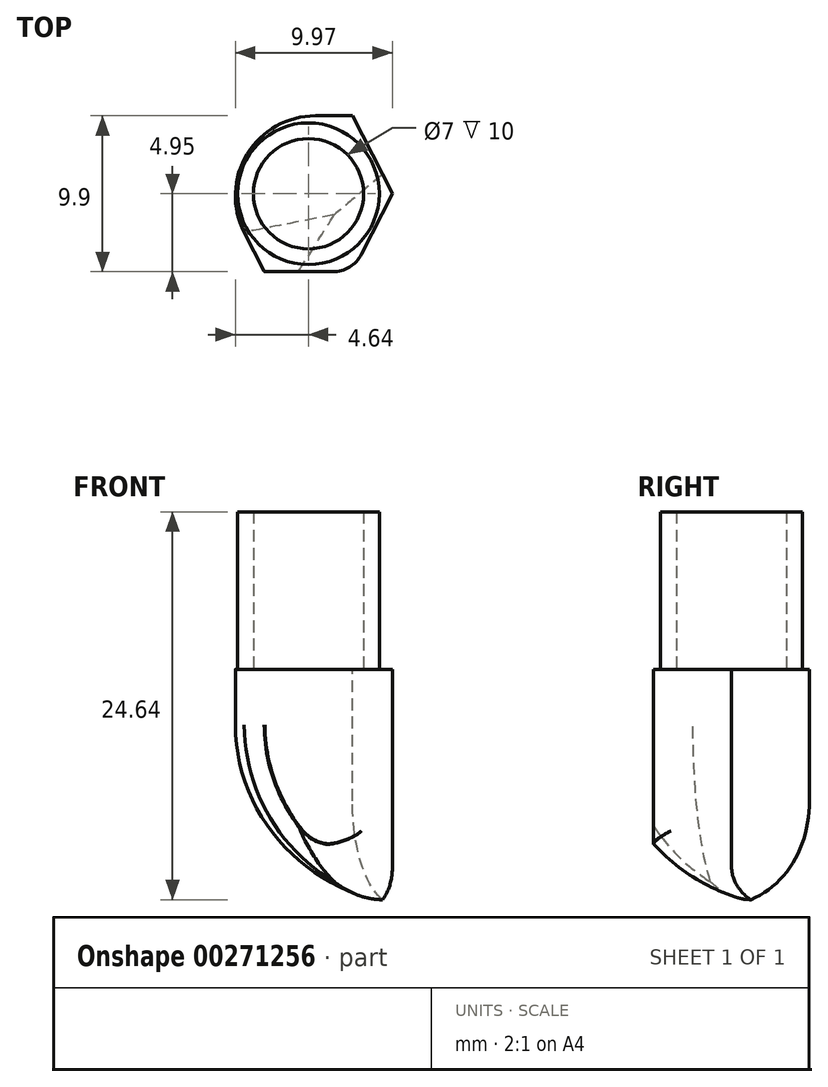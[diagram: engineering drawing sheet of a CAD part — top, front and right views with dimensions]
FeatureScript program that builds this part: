
annotation { "Feature Type Name" : "Feature", "Feature Type Description" : "" }
export const myFeature = defineFeature(function(context is Context, id is Id, definition is map)
    precondition{}
    {
        {
            var Q0;
            Q0=qCreatedBy(makeId("Top.planeOp"),FACE);
            var sketch = newSketch(context, id + "F0", { "sketchPlane" : qUnion([Q0])});
            skCircle(sketch, "E0", {"center": v(0, 0) * mm, "radius": 4.5 * mm});
            skCircle(sketch, "E1.0", {"center": v(0, 0) * mm, "radius": 3.5 * mm});
            skSolve(sketch);
        }
        {
            var Q0;
            Q0 = qSketchRegion(id + "F0", true);
            extrude(context, id + "F1", {"entities" : qUnion([Q0]), "depth" : 10 * mm});
        }
        {
            var Q0;
            Q0=qCreatedBy(makeId("Top.planeOp"),FACE);
            var sketch = newSketch(context, id + "F2", { "sketchPlane" : qUnion([Q0])});
            skLineSegment(sketch, "E2", {"start": v(0, 0) * mm, "end": v(0, -4.95) * mm});
            skLineSegment(sketch, "E3", {"start": v(0, -4.95) * mm, "end": v(0, 0) * mm});
            skLineSegment(sketch, "E4", {"start": v(0, 0) * mm, "end": v(0, 4.95) * mm});
            skLineSegment(sketch, "E5", {"start": v(0, 4.95) * mm, "end": v(2.8, 4.95) * mm});
            skLineSegment(sketch, "E6", {"start": v(2.8, 4.95) * mm, "end": v(2.8, -4.95) * mm});
            skLineSegment(sketch, "E7", {"start": v(2.8, -4.95) * mm, "end": v(0, -4.95) * mm});
            skLineSegment(sketch, "E8", {"start": v(0, -4.95) * mm, "end": v(-2.8, -4.95) * mm});
            skLineSegment(sketch, "E9", {"start": v(-2.8, -4.95) * mm, "end": v(-2.8, 4.95) * mm});
            skLineSegment(sketch, "E10", {"start": v(-2.8, 4.95) * mm, "end": v(0, 4.95) * mm});
            skLineSegment(sketch, "E11", {"start": v(-2.8, 0) * mm, "end": v(-5.33, 0) * mm});
            skLineSegment(sketch, "E12", {"start": v(-5.33, 0) * mm, "end": v(0, 0) * mm});
            skLineSegment(sketch, "E13", {"start": v(2.8, 0) * mm, "end": v(5.33, 0) * mm});
            skPoint(sketch, "E13.endSnap0", {"position": v(2.8, 0) * mm});
            skLineSegment(sketch, "E14", {"start": v(5.33, 0) * mm, "end": v(2.8, 0) * mm});
            skLineSegment(sketch, "E15", {"start": v(-2.8, 4.95) * mm, "end": v(-5.33, 0) * mm});
            skLineSegment(sketch, "E16", {"start": v(-2.8, -4.95) * mm, "end": v(-5.33, 0) * mm});
            skLineSegment(sketch, "E17", {"start": v(2.8, 4.95) * mm, "end": v(5.33, 0) * mm});
            skLineSegment(sketch, "E18", {"start": v(5.33, 0) * mm, "end": v(2.8, -4.95) * mm});
            skSolve(sketch);
        }
        {
            var Q0;
            Q0 = qSketchRegion(id + "F2", true);
            extrude(context, id + "F3", {"entities" : qUnion([Q0]), "operationType" : NewBodyOperationType.ADD, "oppositeDirection" : true, "depth" : 15 * mm});
        }
        {
            var Q0;
            Q0=makeQuery(id+"F3.opExtrude","CAP_EDGE",EDGE,{"disambiguationData":[OSD([sQuery(id+"F2.wireOp",EDGE,"E16")])],"isStart":false});
            fillet(context, id + "F4", {"entities" : qUnion([Q0]), "radius" : 11.65 * mm, "tangentPropagation" : true, "allowEdgeOverflow" : false});
        }
        {
            var Q0;
            Q0=makeQuery(id+"F4.opFillet","BLEND_EDGE",EDGE,{"blendedFrom":[makeQuery(id+"F3.opExtrude","CAP_EDGE",EDGE,{"disambiguationData":[OSD([sQuery(id+"F2.wireOp",EDGE,"E16")])],"isStart":false}),makeQuery(id+"F3.opExtrude","SWEPT_FACE",FACE,{"disambiguationData":[OSD([sQuery(id+"F2.wireOp",EDGE,"E7"),sQuery(id+"F2.wireOp",EDGE,"E8")])]})],"blendedInto":[makeQuery(id+"F3.opExtrude","SWEPT_FACE",FACE,{"disambiguationData":[OSD([sQuery(id+"F2.wireOp",EDGE,"E7"),sQuery(id+"F2.wireOp",EDGE,"E8")])]})]});
            fillet(context, id + "F5", {"entities" : qUnion([Q0]), "radius" : 0.05 * mm, "tangentPropagation" : true, "allowEdgeOverflow" : false});
        }
        {
            var Q0;
            Q0=makeQuery(id+"F4.opFillet","BLEND_EDGE",EDGE,{"blendedFrom":[makeQuery(id+"F3.opExtrude","CAP_EDGE",EDGE,{"disambiguationData":[OSD([sQuery(id+"F2.wireOp",EDGE,"E16")])],"isStart":false}),makeQuery(id+"F3.opExtrude","SWEPT_FACE",FACE,{"disambiguationData":[OSD([sQuery(id+"F2.wireOp",EDGE,"E18")])]})],"blendedInto":[makeQuery(id+"F3.opExtrude","SWEPT_FACE",FACE,{"disambiguationData":[OSD([sQuery(id+"F2.wireOp",EDGE,"E18")])]})]});
            fillet(context, id + "F6", {"entities" : qUnion([Q0]), "radius" : 2.06 * mm, "tangentPropagation" : true, "allowEdgeOverflow" : false});
        }
        {
            var Q0;
            Q0=makeQuery(id+"F4.opFillet","BLEND_EDGE",EDGE,{"blendedFrom":[makeQuery(id+"F3.opExtrude","CAP_EDGE",EDGE,{"disambiguationData":[OSD([sQuery(id+"F2.wireOp",EDGE,"E16")])],"isStart":false}),makeQuery(id+"F3.opExtrude","SWEPT_FACE",FACE,{"disambiguationData":[OSD([sQuery(id+"F2.wireOp",EDGE,"E5"),sQuery(id+"F2.wireOp",EDGE,"E10")])]})],"blendedInto":[makeQuery(id+"F3.opExtrude","SWEPT_FACE",FACE,{"disambiguationData":[OSD([sQuery(id+"F2.wireOp",EDGE,"E5"),sQuery(id+"F2.wireOp",EDGE,"E10")])]})]});
            fillet(context, id + "F7", {"entities" : qUnion([Q0]), "radius" : 5.08 * mm, "tangentPropagation" : true, "allowEdgeOverflow" : false});
        }
    });
